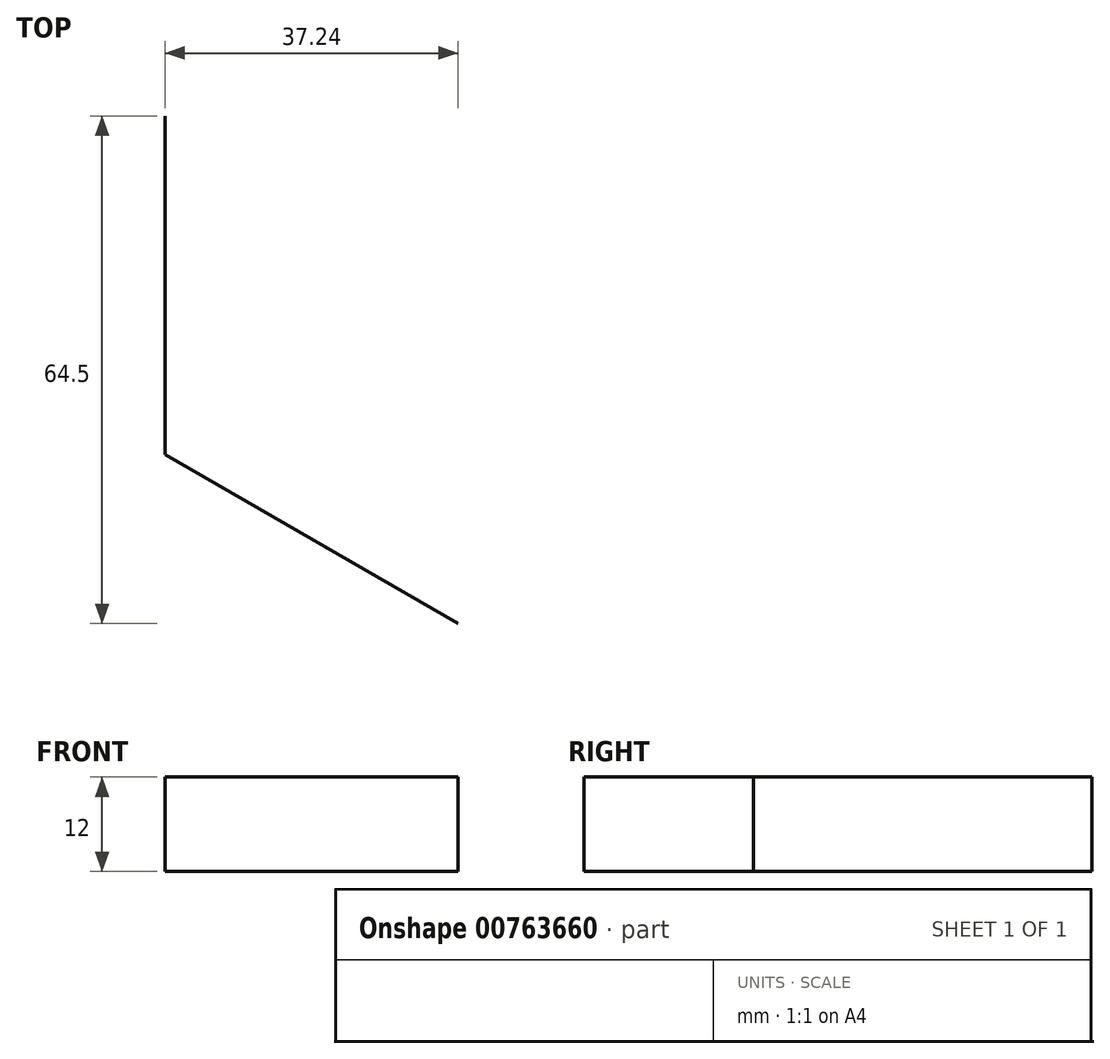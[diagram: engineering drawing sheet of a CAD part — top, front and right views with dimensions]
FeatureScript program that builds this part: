
annotation { "Feature Type Name" : "Feature", "Feature Type Description" : "" }
export const myFeature = defineFeature(function(context is Context, id is Id, definition is map)
    precondition{}
    {
        {
            var Q0;
            Q0=qCreatedBy(makeId("Top.planeOp"),FACE);
            var sketch = newSketch(context, id + "F0", { "sketchPlane" : qUnion([Q0])});
            skLineSegment(sketch, "E0", {"start": v(0, 0) * mm, "end": v(0, 43) * mm});
            skLineSegment(sketch, "E1.1.0", {"start": v(0, 0) * mm, "end": v(-37.24, -21.5) * mm});
            skLineSegment(sketch, "E1.2.0", {"start": v(0, 0) * mm, "end": v(37.24, -21.5) * mm});
            skPoint(sketch, "E1.center", {"position": v(0, 0) * mm});
            skSolve(sketch);
        }
        {
            var Q0;
            Q0=sQuery(id+"F0.wireOp",EDGE,"E0");
            var Q1;
            Q1=sQuery(id+"F0.wireOp",EDGE,"E1.2.0");
            extrude(context, id + "F1", {"bodyType" : ToolBodyType.SURFACE, "surfaceEntities" : qUnion([Q0, Q1]), "depth" : 12 * mm, "offsetDistance" : 25 * mm});
        }
    });
